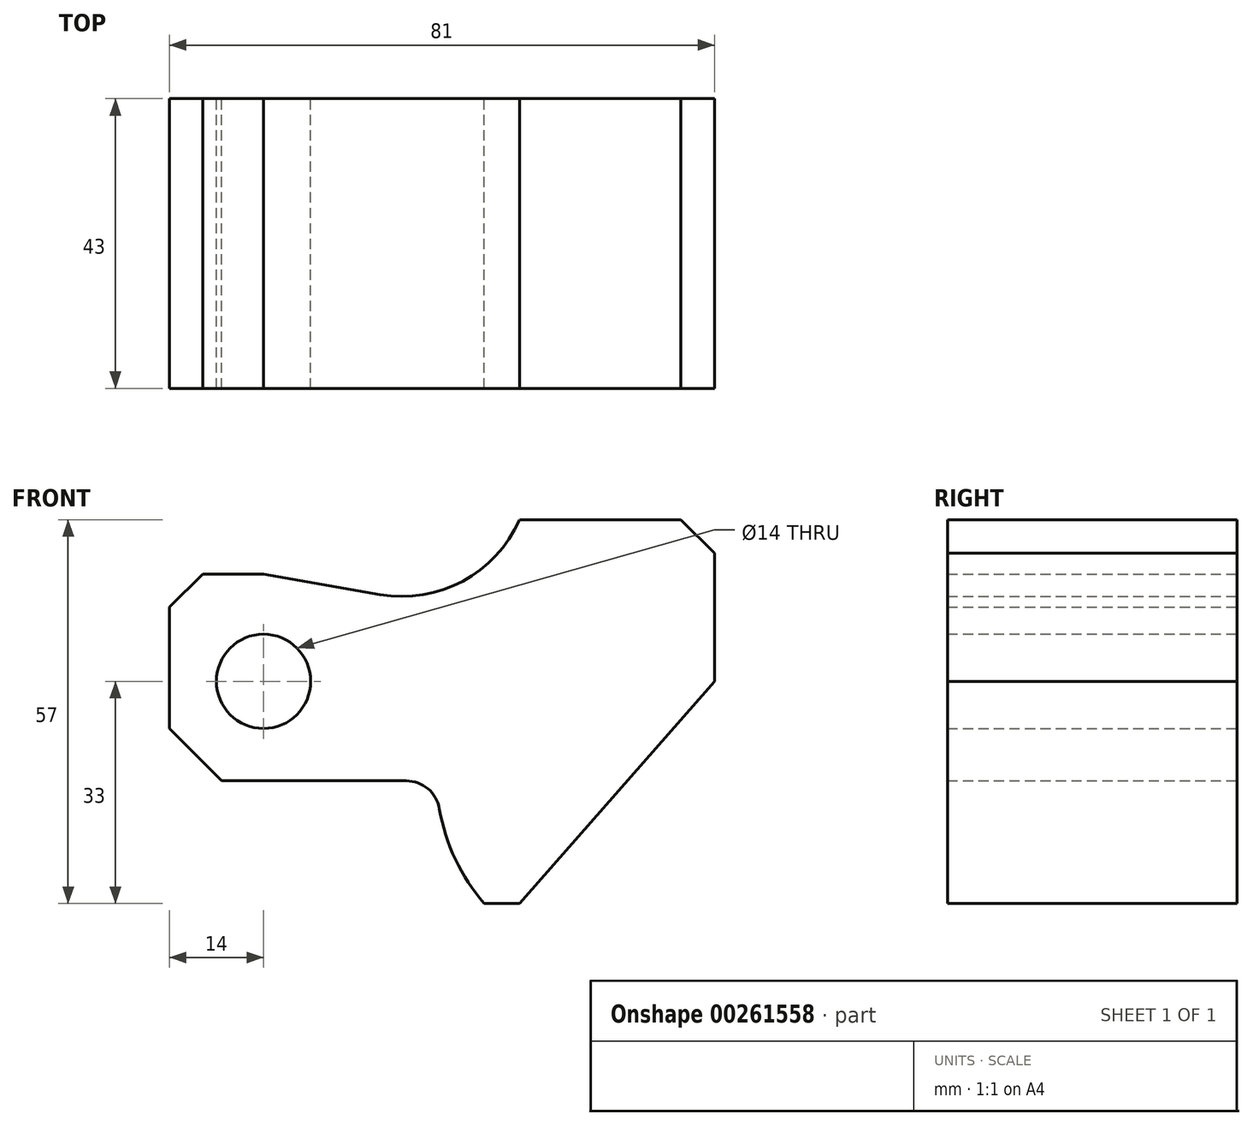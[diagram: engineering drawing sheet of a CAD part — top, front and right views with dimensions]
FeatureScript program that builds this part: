
annotation { "Feature Type Name" : "Feature", "Feature Type Description" : "" }
export const myFeature = defineFeature(function(context is Context, id is Id, definition is map)
    precondition{}
    {
        {
            var Q0;
            Q0=qCreatedBy(makeId("Front.planeOp"),FACE);
            var sketch = newSketch(context, id + "F0", { "sketchPlane" : qUnion([Q0])});
            skCircle(sketch, "E0", {"center": v(0, 0) * mm, "radius": 7 * mm});
            skPoint(sketch, "E1", {"position": v(-14, 0) * mm});
            skLineSegment(sketch, "E2", {"start": v(-14, 0) * mm, "end": v(-14, -7) * mm});
            skLineSegment(sketch, "E3", {"start": v(-14, 0) * mm, "end": v(-14, 11) * mm});
            skLineSegment(sketch, "E4", {"start": v(-14, 11) * mm, "end": v(-9.05, 15.95) * mm});
            skLineSegment(sketch, "E5", {"start": v(-14, -7) * mm, "end": v(-6.22, -14.78) * mm});
            skLineSegment(sketch, "E6", {"start": v(-9.05, 15.95) * mm, "end": v(0, 15.95) * mm});
            skPoint(sketch, "E7", {"position": v(67, 0) * mm});
            skLineSegment(sketch, "E8", {"start": v(67, 0) * mm, "end": v(67, 19) * mm});
            skLineSegment(sketch, "E9", {"start": v(67, 19) * mm, "end": v(62, 24) * mm});
            skLineSegment(sketch, "E10", {"start": v(62, 24) * mm, "end": v(38, 24) * mm});
            skArc(sketch, "E11", {"start": v(17.3, 12.9) * mm, "mid": v(29.57, 14.87) * mm, "end": v(38, 24) * mm});
            skLineSegment(sketch, "E12", {"start": v(0, 15.95) * mm, "end": v(17.3, 12.9) * mm});
            skLineSegment(sketch, "E13", {"start": v(-6.22, -14.78) * mm, "end": v(21.2, -14.78) * mm});
            skArc(sketch, "E14", {"start": v(26.12, -18.93) * mm, "mid": v(24.41, -15.95) * mm, "end": v(21.2, -14.78) * mm});
            skLineSegment(sketch, "E15", {"start": v(67, 0) * mm, "end": v(67, -33) * mm, "construction": true});
            skLineSegment(sketch, "E16", {"start": v(67, -33) * mm, "end": v(38, -33) * mm, "construction": true});
            skLineSegment(sketch, "E17", {"start": v(67, 0) * mm, "end": v(38, -33) * mm});
            skLineSegment(sketch, "E18", {"start": v(54.7, -14) * mm, "end": v(54.7, -33) * mm, "construction": true});
            skLineSegment(sketch, "E19", {"start": v(38, -33) * mm, "end": v(32.79, -33) * mm});
            skArc(sketch, "E20", {"start": v(26.12, -18.93) * mm, "mid": v(28.5, -26.42) * mm, "end": v(32.79, -33) * mm});
            skSolve(sketch);
        }
        {
            var Q0;
            Q0 = qSketchRegion(id + "F0", true);
            extrude(context, id + "F1", {"entities" : qUnion([Q0]), "depth" : 43 * mm});
        }
    });
